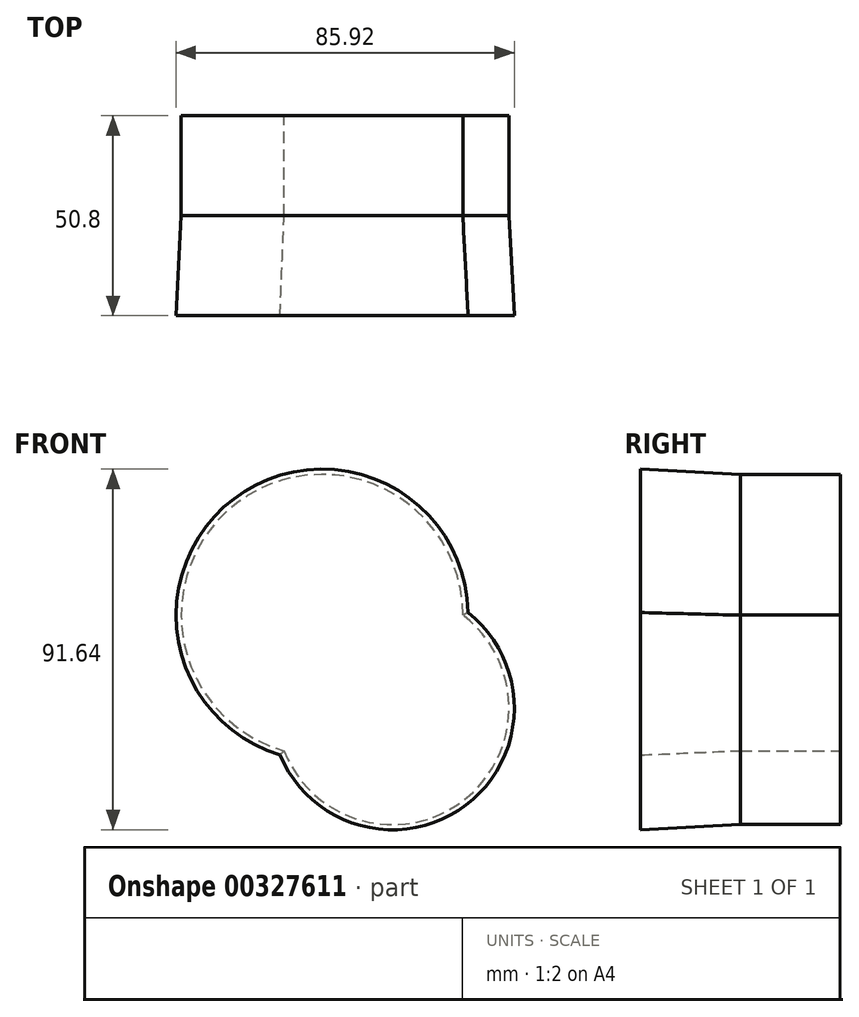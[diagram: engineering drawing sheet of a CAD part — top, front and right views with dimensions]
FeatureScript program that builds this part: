
annotation { "Feature Type Name" : "Feature", "Feature Type Description" : "" }
export const myFeature = defineFeature(function(context is Context, id is Id, definition is map)
    precondition{}
    {
        {
            var Q0;
            Q0=qCreatedBy(makeId("Front.planeOp"),FACE);
            var sketch = newSketch(context, id + "F0", { "sketchPlane" : qUnion([Q0])});
            skCircle(sketch, "E0", {"center": v(0, 0) * mm, "radius": 35.76 * mm});
            skCircle(sketch, "E1", {"center": v(17.88, -23.6) * mm, "radius": 29.6 * mm});
            skPoint(sketch, "E1.second.point", {"position": v(38.35, -45) * mm});
            skPoint(sketch, "E1.third.point", {"position": v(35.76, 0) * mm});
            skSolve(sketch);
        }
        {
            var Q0;
            Q0 = qSketchRegion(id + "F0", true);
            extrude(context, id + "F1", {"entities" : qUnion([Q0]), "depth" : 25.4 * mm, "hasDraft" : true, "draftAngle" : 3 * degree, "hasSecondDirection" : true, "secondDirectionOppositeDirection" : true, "secondDirectionDepth" : 25.4 * mm});
        }
    });
